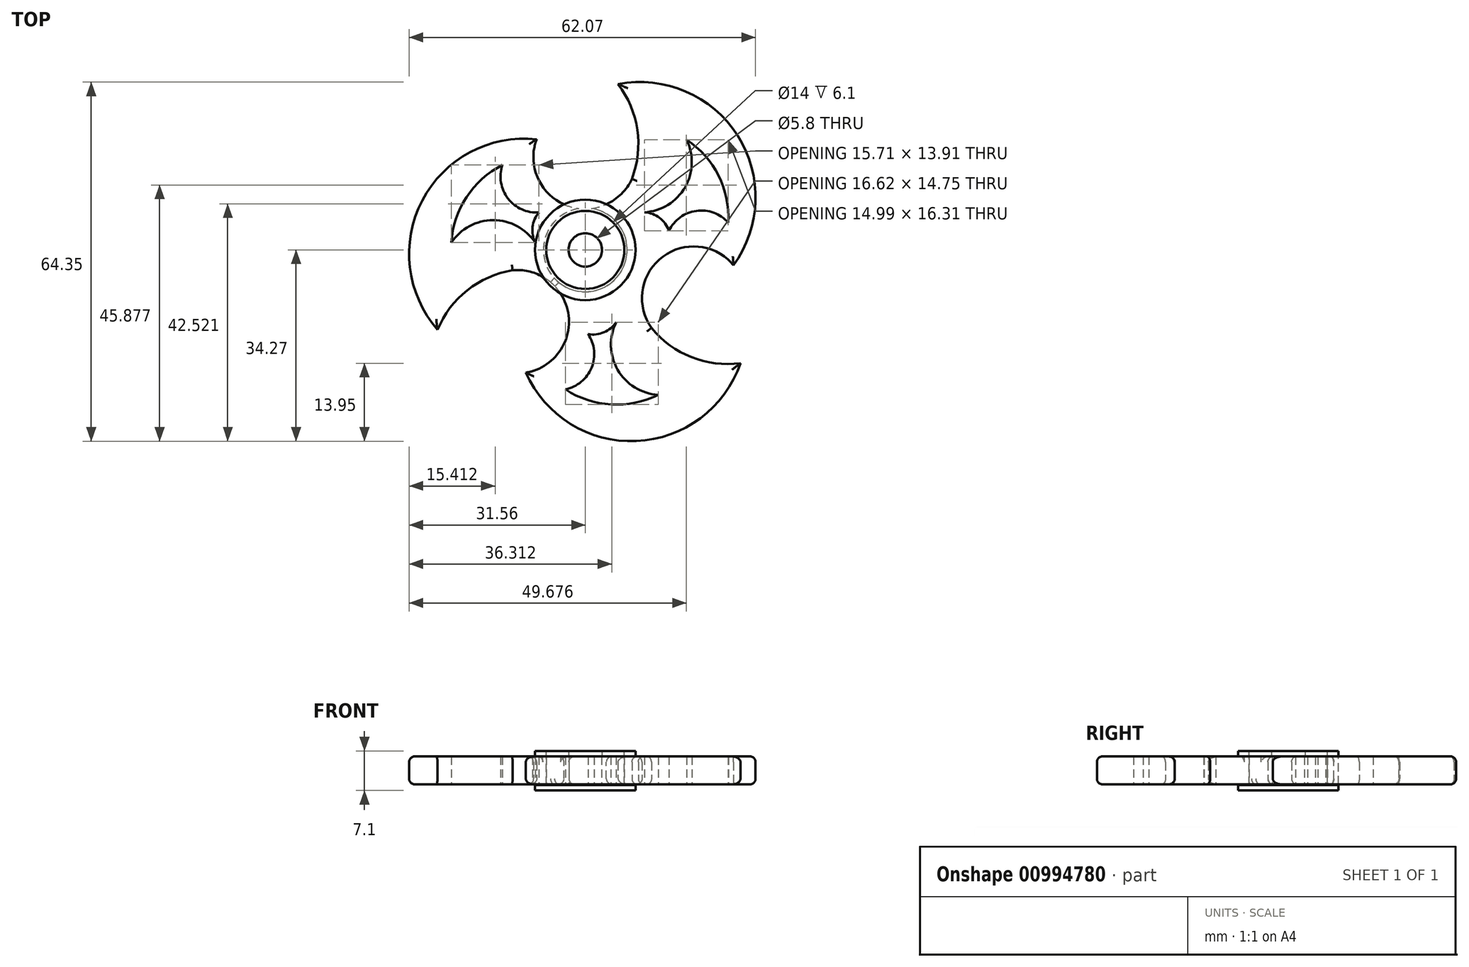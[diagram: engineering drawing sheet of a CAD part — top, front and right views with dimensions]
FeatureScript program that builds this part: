
annotation { "Feature Type Name" : "Feature", "Feature Type Description" : "" }
export const myFeature = defineFeature(function(context is Context, id is Id, definition is map)
    precondition{}
    {
        {
            var Q0;
            Q0=qCreatedBy(makeId("Top.planeOp"),FACE);
            var sketch = newSketch(context, id + "F0", { "sketchPlane" : qUnion([Q0])});
            skCircle(sketch, "E0", {"center": v(0, 0) * mm, "radius": 7.5 * mm});
            skArc(sketch, "E1", {"start": v(-9.11, 18.47) * mm, "mid": v(-2.93, 7.81) * mm, "end": v(8.36, 12.73) * mm});
            skArc(sketch, "E2", {"start": v(-8.7, 19.83) * mm, "mid": v(-8.93, 19.16) * mm, "end": v(-9.11, 18.47) * mm});
            skArc(sketch, "E3", {"start": v(-8.7, 19.83) * mm, "mid": v(-29.22, 8.83) * mm, "end": v(-26.47, -14.3) * mm});
            skArc(sketch, "E4", {"start": v(-13.02, -3.65) * mm, "mid": v(-21.13, -7.23) * mm, "end": v(-26.47, -14.3) * mm});
            skArc(sketch, "E5", {"start": v(-3.68, -16.56) * mm, "mid": v(-4.68, -7.44) * mm, "end": v(-13.02, -3.65) * mm});
            skArc(sketch, "E6", {"start": v(-14.85, 15.2) * mm, "mid": v(-21.28, 9.47) * mm, "end": v(-24, 1.3) * mm});
            skArc(sketch, "E7", {"start": v(-14.85, 15.2) * mm, "mid": v(-13.83, 9.22) * mm, "end": v(-8.3, 6.72) * mm});
            skArc(sketch, "E8", {"start": v(-8.97, 1.3) * mm, "mid": v(-16.49, 5.34) * mm, "end": v(-24, 1.3) * mm});
            skArc(sketch, "E9", {"start": v(-8.3, 6.72) * mm, "mid": v(-9.45, 4.1) * mm, "end": v(-8.97, 1.3) * mm});
            skArc(sketch, "E10.1.0", {"start": v(-3.56, -25) * mm, "mid": v(4.62, -27.7) * mm, "end": v(13.06, -25.96) * mm});
            skArc(sketch, "E10.1.1", {"start": v(18.36, 0.56) * mm, "mid": v(10.97, -4.86) * mm, "end": v(11.86, -13.98) * mm});
            skArc(sketch, "E10.1.2", {"start": v(5.55, -12.95) * mm, "mid": v(5.8, -21.47) * mm, "end": v(13.06, -25.96) * mm});
            skArc(sketch, "E10.1.3", {"start": v(-10.65, -21.97) * mm, "mid": v(9.14, -34.25) * mm, "end": v(27.8, -20.3) * mm});
            skArc(sketch, "E10.1.4", {"start": v(-3.56, -25) * mm, "mid": v(1.12, -21.12) * mm, "end": v(0.51, -15.07) * mm});
            skPoint(sketch, "E10.1.5", {"position": v(2.18, -4.53) * mm});
            skArc(sketch, "E10.1.6", {"start": v(11.86, -13.98) * mm, "mid": v(19, -19.21) * mm, "end": v(27.8, -20.3) * mm});
            skArc(sketch, "E10.1.7", {"start": v(-9.26, -21.66) * mm, "mid": v(-3.12, -10.98) * mm, "end": v(-13.02, -3.65) * mm});
            skArc(sketch, "E10.1.8", {"start": v(0.51, -15.07) * mm, "mid": v(3.35, -14.77) * mm, "end": v(5.55, -12.95) * mm});
            skPoint(sketch, "E10.1.9", {"position": v(2.18, -4.53) * mm});
            skArc(sketch, "E10.1.10", {"start": v(-10.65, -21.97) * mm, "mid": v(-9.95, -21.85) * mm, "end": v(-9.26, -21.66) * mm});
            skArc(sketch, "E10.2.0", {"start": v(25.61, 4.89) * mm, "mid": v(23.86, 13.32) * mm, "end": v(18.14, 19.76) * mm});
            skArc(sketch, "E10.2.1", {"start": v(-7.48, 11.1) * mm, "mid": v(0.9, 7.4) * mm, "end": v(8.36, 12.73) * mm});
            skArc(sketch, "E10.2.2", {"start": v(10.62, 6.75) * mm, "mid": v(17.88, 11.24) * mm, "end": v(18.14, 19.76) * mm});
            skArc(sketch, "E10.2.3", {"start": v(26.54, -2.76) * mm, "mid": v(27.27, 20.51) * mm, "end": v(5.88, 29.7) * mm});
            skArc(sketch, "E10.2.4", {"start": v(25.61, 4.89) * mm, "mid": v(19.91, 7) * mm, "end": v(14.98, 3.45) * mm});
            skPoint(sketch, "E10.2.5", {"position": v(5.02, -0.37) * mm});
            skArc(sketch, "E10.2.6", {"start": v(8.36, 12.73) * mm, "mid": v(9.32, 21.54) * mm, "end": v(5.88, 29.7) * mm});
            skArc(sketch, "E10.2.7", {"start": v(25.57, -1.72) * mm, "mid": v(13.25, -1.74) * mm, "end": v(11.86, -13.98) * mm});
            skArc(sketch, "E10.2.8", {"start": v(14.98, 3.45) * mm, "mid": v(13.3, 5.76) * mm, "end": v(10.62, 6.75) * mm});
            skPoint(sketch, "E10.2.9", {"position": v(5.02, -0.37) * mm});
            skArc(sketch, "E10.2.10", {"start": v(26.54, -2.76) * mm, "mid": v(26.08, -2.22) * mm, "end": v(25.57, -1.72) * mm});
            skPoint(sketch, "E10.center", {"position": v(2.4, -1.63) * mm});
            skSolve(sketch);
        }
        {
            var Q0;
            Q0=makeQuery(id+"F0.imprint","IMPRINT",FACE,{"disambiguationData":[TD([[makeQuery(id+"F0.imprint","IMPRINT",EDGE,{"derivedFrom":sQuery(id+"F0.wireOp",EDGE,"E0")}),-1.0]])]});
            extrude(context, id + "F1", {"entities" : qUnion([Q0]), "depth" : 5 * mm, "offsetDistance" : 25 * mm});
        }
        {
            var Q0;
            Q0=makeQuery(id+"F1.opExtrude","CAP_FACE",FACE,{"disambiguationData":[OSD([sQuery(id+"F0.wireOp",EDGE,"E0"),sQuery(id+"F0.wireOp",EDGE,"E1"),sQuery(id+"F0.wireOp",EDGE,"E2"),sQuery(id+"F0.wireOp",EDGE,"E3"),sQuery(id+"F0.wireOp",EDGE,"E4"),sQuery(id+"F0.wireOp",EDGE,"E6"),sQuery(id+"F0.wireOp",EDGE,"E7"),sQuery(id+"F0.wireOp",EDGE,"E8"),sQuery(id+"F0.wireOp",EDGE,"E9"),sQuery(id+"F0.wireOp",EDGE,"E10.1.0"),sQuery(id+"F0.wireOp",EDGE,"E10.1.2"),sQuery(id+"F0.wireOp",EDGE,"E10.1.3"),sQuery(id+"F0.wireOp",EDGE,"E10.1.4"),sQuery(id+"F0.wireOp",EDGE,"E10.1.6"),sQuery(id+"F0.wireOp",EDGE,"E10.1.7"),sQuery(id+"F0.wireOp",EDGE,"E10.1.8"),sQuery(id+"F0.wireOp",EDGE,"E10.1.10"),sQuery(id+"F0.wireOp",EDGE,"E10.2.0"),sQuery(id+"F0.wireOp",EDGE,"E10.2.1"),sQuery(id+"F0.wireOp",EDGE,"E10.2.2"),sQuery(id+"F0.wireOp",EDGE,"E10.2.3"),sQuery(id+"F0.wireOp",EDGE,"E10.2.4"),sQuery(id+"F0.wireOp",EDGE,"E10.2.6"),sQuery(id+"F0.wireOp",EDGE,"E10.2.7"),sQuery(id+"F0.wireOp",EDGE,"E10.2.8"),sQuery(id+"F0.wireOp",EDGE,"E10.2.10")])],"isStart":false});
            var sketch = newSketch(context, id + "F2", { "sketchPlane" : qUnion([Q0])});
            skCircle(sketch, "E11.0", {"center": v(0, 0) * mm, "radius": 7 * mm});
            skCircle(sketch, "E12", {"center": v(0, 0) * mm, "radius": 3 * mm});
            skCircle(sketch, "E13.0", {"center": v(0, 0) * mm, "radius": 9 * mm});
            skSolve(sketch);
        }
        {
            var Q0;
            Q0=makeQuery(id+"F2.imprint","IMPRINT",FACE,{"disambiguationData":[TD([[makeQuery(id+"F2.imprint","IMPRINT",EDGE,{"derivedFrom":sQuery(id+"F2.wireOp",EDGE,"E11.0")}),-1.0]])]});
            extrude(context, id + "F3", {"entities" : qUnion([Q0]), "oppositeDirection" : true, "depth" : 5.1 * mm, "offsetDistance" : 25 * mm});
        }
        {
            var Q0;
            Q0=qSketchRegion(id+"F2",true);
            var Q1;
            Q1=makeQuery(id+"F2.imprint","IMPRINT",FACE,{"disambiguationData":[TD([[makeQuery(id+"F2.imprint","IMPRINT",EDGE,{"derivedFrom":sQuery(id+"F2.wireOp",EDGE,"E11.0")}),-1.0]])]});
            var Q2;
            Q2=makeQuery(id+"F2.imprint","IMPRINT",FACE,{"disambiguationData":[TD([[makeQuery(id+"F2.imprint","IMPRINT",EDGE,{"derivedFrom":sQuery(id+"F2.wireOp",EDGE,"E12")}),1.0]])]});
            var Q3;
            Q3=sQuery(id+"F0.wireOp",EDGE,"E0");
            extrude(context, id + "F4", {"entities" : qUnion([Q0, Q1, Q2]), "operationType" : NewBodyOperationType.ADD, "surfaceOperationType" : NewSurfaceOperationType.ADD, "surfaceEntities" : qUnion([Q3]), "depth" : 1 * mm, "offsetDistance" : 25 * mm});
        }
        {
            var Q0;
            Q0=makeQuery(id+"F3.opExtrude","CAP_FACE",FACE,{"disambiguationData":[OSD([sQuery(id+"F2.wireOp",EDGE,"E11.0"),sQuery(id+"F2.wireOp",EDGE,"E12")])],"isStart":false});
            var sketch = newSketch(context, id + "F5", { "sketchPlane" : qUnion([Q0])});
            skCircle(sketch, "E14.0", {"center": v(0, 0) * mm, "radius": 2.9 * mm});
            skCircle(sketch, "E15.0", {"center": v(0, 0) * mm, "radius": 9 * mm});
            skSolve(sketch);
        }
        {
            var Q0;
            Q0=makeQuery(id+"F5.imprint","IMPRINT",FACE,{"disambiguationData":[TD([[makeQuery(id+"F5.imprint","IMPRINT",EDGE,{"derivedFrom":sQuery(id+"F5.wireOp",EDGE,"E14.0")}),-1.0]])]});
            var Q1;
            Q1=makeQuery(id+"F1.opExtrude","CAP_FACE",FACE,{"disambiguationData":[OSD([sQuery(id+"F0.wireOp",EDGE,"E0"),sQuery(id+"F0.wireOp",EDGE,"E1"),sQuery(id+"F0.wireOp",EDGE,"E2"),sQuery(id+"F0.wireOp",EDGE,"E3"),sQuery(id+"F0.wireOp",EDGE,"E4"),sQuery(id+"F0.wireOp",EDGE,"E6"),sQuery(id+"F0.wireOp",EDGE,"E7"),sQuery(id+"F0.wireOp",EDGE,"E8"),sQuery(id+"F0.wireOp",EDGE,"E9"),sQuery(id+"F0.wireOp",EDGE,"E10.1.0"),sQuery(id+"F0.wireOp",EDGE,"E10.1.2"),sQuery(id+"F0.wireOp",EDGE,"E10.1.3"),sQuery(id+"F0.wireOp",EDGE,"E10.1.4"),sQuery(id+"F0.wireOp",EDGE,"E10.1.6"),sQuery(id+"F0.wireOp",EDGE,"E10.1.7"),sQuery(id+"F0.wireOp",EDGE,"E10.1.8"),sQuery(id+"F0.wireOp",EDGE,"E10.1.10"),sQuery(id+"F0.wireOp",EDGE,"E10.2.0"),sQuery(id+"F0.wireOp",EDGE,"E10.2.1"),sQuery(id+"F0.wireOp",EDGE,"E10.2.2"),sQuery(id+"F0.wireOp",EDGE,"E10.2.3"),sQuery(id+"F0.wireOp",EDGE,"E10.2.4"),sQuery(id+"F0.wireOp",EDGE,"E10.2.6"),sQuery(id+"F0.wireOp",EDGE,"E10.2.7"),sQuery(id+"F0.wireOp",EDGE,"E10.2.8"),sQuery(id+"F0.wireOp",EDGE,"E10.2.10")])],"isStart":false});
            extrude(context, id + "F6", {"entities" : qUnion([Q0]), "endBound" : BoundingType.UP_TO_SURFACE, "oppositeDirection" : true, "depth" : 25 * mm, "endBoundEntityFace" : qUnion([Q1]), "offsetDistance" : 25 * mm});
        }
        {
            var Q0;
            Q0=makeQuery(id+"F5.imprint","IMPRINT",FACE,{"disambiguationData":[TD([[makeQuery(id+"F5.imprint","IMPRINT",EDGE,{"derivedFrom":sQuery(id+"F5.wireOp",EDGE,"E15.0")}),1.0]])]});
            var Q1;
            Q1=makeQuery(id+"F5.imprint","IMPRINT",FACE,{"disambiguationData":[TD([[makeQuery(id+"F5.imprint","IMPRINT",EDGE,{"derivedFrom":makeQuery(id+"F3.opExtrude","CAP_EDGE",EDGE,{"disambiguationData":[OSD([sQuery(id+"F2.wireOp",EDGE,"E11.0")])],"isStart":false})}),1.0]])]});
            var Q2;
            Q2=makeQuery(id+"F5.imprint","IMPRINT",FACE,{"disambiguationData":[TD([[makeQuery(id+"F5.imprint","IMPRINT",EDGE,{"derivedFrom":sQuery(id+"F5.wireOp",EDGE,"E14.0")}),-1.0]])]});
            var Q3;
            Q3=makeQuery(id+"F5.imprint","IMPRINT",FACE,{"disambiguationData":[TD([[makeQuery(id+"F5.imprint","IMPRINT",EDGE,{"derivedFrom":sQuery(id+"F5.wireOp",EDGE,"E14.0")}),1.0]])]});
            extrude(context, id + "F7", {"entities" : qUnion([Q0, Q1, Q2, Q3]), "depth" : 1 * mm, "offsetDistance" : 25 * mm});
        }
        {
            var Q0;
            Q0=makeQuery(id+"F1.opExtrude","CAP_EDGE",EDGE,{"disambiguationData":[OSD([sQuery(id+"F0.wireOp",EDGE,"E10.1.3")])],"isStart":true});
            var Q1;
            Q1=makeQuery(id+"F1.opExtrude","CAP_EDGE",EDGE,{"disambiguationData":[OSD([sQuery(id+"F0.wireOp",EDGE,"E10.1.6")])],"isStart":true});
            var Q2;
            Q2=makeQuery(id+"F1.opExtrude","CAP_EDGE",EDGE,{"disambiguationData":[OSD([sQuery(id+"F0.wireOp",EDGE,"E10.2.7")])],"isStart":true});
            var Q3;
            Q3=makeQuery(id+"F1.opExtrude","CAP_EDGE",EDGE,{"disambiguationData":[OSD([sQuery(id+"F0.wireOp",EDGE,"E10.2.3")])],"isStart":true});
            var Q4;
            Q4=makeQuery(id+"F1.opExtrude","CAP_EDGE",EDGE,{"disambiguationData":[OSD([sQuery(id+"F0.wireOp",EDGE,"E10.2.6")])],"isStart":true});
            var Q5;
            Q5=makeQuery(id+"F1.opExtrude","CAP_EDGE",EDGE,{"disambiguationData":[OSD([sQuery(id+"F0.wireOp",EDGE,"E1"),sQuery(id+"F0.wireOp",EDGE,"E10.2.1")])],"isStart":true});
            var Q6;
            Q6=makeQuery(id+"F1.opExtrude","CAP_EDGE",EDGE,{"disambiguationData":[OSD([sQuery(id+"F0.wireOp",EDGE,"E3")])],"isStart":true});
            var Q7;
            Q7=makeQuery(id+"F1.opExtrude","CAP_EDGE",EDGE,{"disambiguationData":[OSD([sQuery(id+"F0.wireOp",EDGE,"E4")])],"isStart":true});
            var Q8;
            Q8=makeQuery(id+"F1.opExtrude","CAP_EDGE",EDGE,{"disambiguationData":[OSD([sQuery(id+"F0.wireOp",EDGE,"E10.1.7")])],"isStart":true});
            var Q9;
            Q9=makeQuery(id+"F1.opExtrude","CAP_EDGE",EDGE,{"disambiguationData":[OSD([sQuery(id+"F0.wireOp",EDGE,"E3")])],"isStart":false});
            var Q10;
            Q10=makeQuery(id+"F1.opExtrude","CAP_EDGE",EDGE,{"disambiguationData":[OSD([sQuery(id+"F0.wireOp",EDGE,"E1"),sQuery(id+"F0.wireOp",EDGE,"E10.2.1")])],"isStart":false});
            var Q11;
            Q11=makeQuery(id+"F1.opExtrude","CAP_EDGE",EDGE,{"disambiguationData":[OSD([sQuery(id+"F0.wireOp",EDGE,"E10.2.1")])],"isStart":false});
            var Q12;
            Q12=makeQuery(id+"F1.opExtrude","CAP_EDGE",EDGE,{"disambiguationData":[OSD([sQuery(id+"F0.wireOp",EDGE,"E10.2.6")])],"isStart":false});
            var Q13;
            Q13=makeQuery(id+"F1.opExtrude","CAP_EDGE",EDGE,{"disambiguationData":[OSD([sQuery(id+"F0.wireOp",EDGE,"E10.2.3")])],"isStart":false});
            var Q14;
            Q14=makeQuery(id+"F1.opExtrude","CAP_EDGE",EDGE,{"disambiguationData":[OSD([sQuery(id+"F0.wireOp",EDGE,"E10.2.7")])],"isStart":false});
            var Q15;
            Q15=makeQuery(id+"F1.opExtrude","CAP_EDGE",EDGE,{"disambiguationData":[OSD([sQuery(id+"F0.wireOp",EDGE,"E10.1.6")])],"isStart":false});
            var Q16;
            Q16=makeQuery(id+"F1.opExtrude","CAP_EDGE",EDGE,{"disambiguationData":[OSD([sQuery(id+"F0.wireOp",EDGE,"E10.1.3")])],"isStart":false});
            var Q17;
            Q17=makeQuery(id+"F1.opExtrude","CAP_EDGE",EDGE,{"disambiguationData":[OSD([sQuery(id+"F0.wireOp",EDGE,"E10.1.7")])],"isStart":false});
            var Q18;
            Q18=makeQuery(id+"F1.opExtrude","CAP_EDGE",EDGE,{"disambiguationData":[OSD([sQuery(id+"F0.wireOp",EDGE,"E4")])],"isStart":false});
            fillet(context, id + "F8", {"entities" : qUnion([Q0, Q1, Q2, Q3, Q4, Q5, Q6, Q7, Q8, Q9, Q10, Q11, Q12, Q13, Q14, Q15, Q16, Q17, Q18]), "radius" : 1 * mm, "tangentPropagation" : true, "allowEdgeOverflow" : false});
        }
    });
